# Revit family: IS_Idealrain_Multiproduct_BIM_GB_B9829;B9830;B9838;B9840
name_source: partatom
category: Plumbing Fixtures
revit_build: Autodesk Revit MEP 2014 (Build: 20130308_1515(x64)
units: mm (PartAtom-declared; Revit-internal decimal feet)

## types (4) — shared parameters
Accessories = www.idealspec.co.uk
AreaUnits = millimeters
Assembly Code = C1030200
AssetType = Fixed
BREEAMApproved = No
Brand = Ideal Standard
ChromeMtl = ISI_IdealStandard_Brassware_Chrome_Render
Color = Chrome
ConnectionType = Plumbing
Default Elevation = 800 mm
DurationUnit = year
ECA = No
ExpectedLife = 30
FaucetFunction = MIXED
FaucetOperation = LEVERHANDLE
Finish = Chrome
Help = www.idealspec.co.uk/contact-us.html
IfcExportAs = IfcValveType
IfcExportType = SHOWERS
InstallationInstructions = www.idealspec.co.uk/resources.html
LinearUnits = millimeters
ManufacturerURL = www.idealspec.co.uk
Material = Brass
NBSDescription = Shower Fittings Package
NBSReference = 45-35-70/330
Name = ShowerMixers_IdealRain_A5691AA_IdealStandard
PlasticMtl = ISI_IdealStandard_Brassware_Plastic_Render
Shape = Sculptured
Space = Internal
SpareParts = www.fastpart-spares.co.uk
TMV3 = Yes
TestPressure = 10 Bar
URL = www.idealspec.co.uk
Uniclass2015Code = Pr_40_20_87_75
Uniclass2015Title = Shower Fittings Package
Uniclass2015Version = Product v1.1
Version = 1
VolumeUnits = Litres
WRAS = Yes
WarrantyDescription = Manufacturers Warranty
WarrantyDurationParts = 5
WarrantyDurationUnit = year
WaterEfficientProduct = No
WorkingPressure = 3 Bar
zero-valued in all types: CWFU, Cost, HWFU, NominalHeight, WFU

## per-type parameters (varying)
| type | 120mm | 80mm | BIMObjectName | BarCode | Description | Features | FlowRate | Model | NettWeight | NominalLength | NominalWidth | ProductInformation | Size |
| B9838AA - Idealrain Pro L3 - Shower Kit - 3 Funtions - 120mm Handspray - 600mm Rail - 1750mm Hose | Yes | No | ISI_IdealStandard_ShowerMixers_IdealRain_B9838AA | 3800861030140 | Idealrain Pro L3 shower kit with 3 function 120mm handspray, 600mm rail and 1750mm hose | Pro L3 shower kit with 3 function 120mm handspray, 600mm rail and 1750mm hose | 8L/min @ 3bar | B9838AA | 1.63Kg | 605 mm  [stored 1.98491 ft] | 120 mm | www.idealspec.co.uk/assets/datasheet/B9838AA | 0 x 605 x 120 mm |
| B9829AA - Idealrain Pro S1 - Shower Kit - 1 Funtion - 80mm Handspray - 600mm Rail - 1750mm Hose | No | Yes | ISI_IdealStandard_ShowerMixers_IdealRain_B9829AA | 3800861030058 | Idealrain Pro S1 shower kit 1 with single function ø80mm handspray, 600mm rail and 1750mm hose | Pro S1 shower kit 1 with single function ø80mm handspray, 600mm rail and 1750mm hose |  | B9829AA | 1.48Kg | 605 mm  [stored 1.98491 ft] | 80 mm  [stored 0.262467 ft] | www.idealspec.co.uk/assets/datasheet/B9829AA | 0 x 605 x 80 mm |
| B9830AA - Idealrain Pro S3 - Shower Kit - 3 Funtion - 80mm Handspray - 600mm Rail - 1750mm Hose | No | Yes | ISI_IdealStandard_ShowerMixers_IdealRain_B9830AA | 3800861030065 | Idealrain Pro S3 shower kit with 3 function ø80mm handspray, 600mm rail and 1750mm hose | Pro S3 shower kit with 3 function ø80mm handspray, 600mm rail and 1750mm hose | 8L/min @ 3bar | B9830AA | 1.52Kg | 605 mm  [stored 1.98491 ft] | 80 mm  [stored 0.262467 ft] | www.idealspec.co.uk/assets/datasheet/B9830AA | 0 x 605 x 80 mm |
| B9840AA - Idealrain Pro L3 - Shower Kit - 3 Funtions - 120mm Handspray - 900mm Rail - 1750mm Hose | Yes | No | ISI_IdealStandard_ShowerMixers_IdealRain_B9840AA | 3800861030164 | Idealrain Pro L3 shower kit with 3 function 120mm handspray, 900mm rail and 1750mm hose | Pro L3 shower kit with 3 function 120mm handspray, 900mm rail and 1750mm hose | 8L/min @ 3bar | B9840AA | 1.91Kg | 900 mm | 120 mm | www.idealspec.co.uk/assets/datasheet/B9840AA | 0 x 900 x 120 mm |

note: [stored X ft] marks values corroborated as IEEE doubles in the binary element streams (Revit-internal decimal feet)

## geometry (parser evidence)
native form markers: Sweep x2
no freeform markers — native parametric forms only
